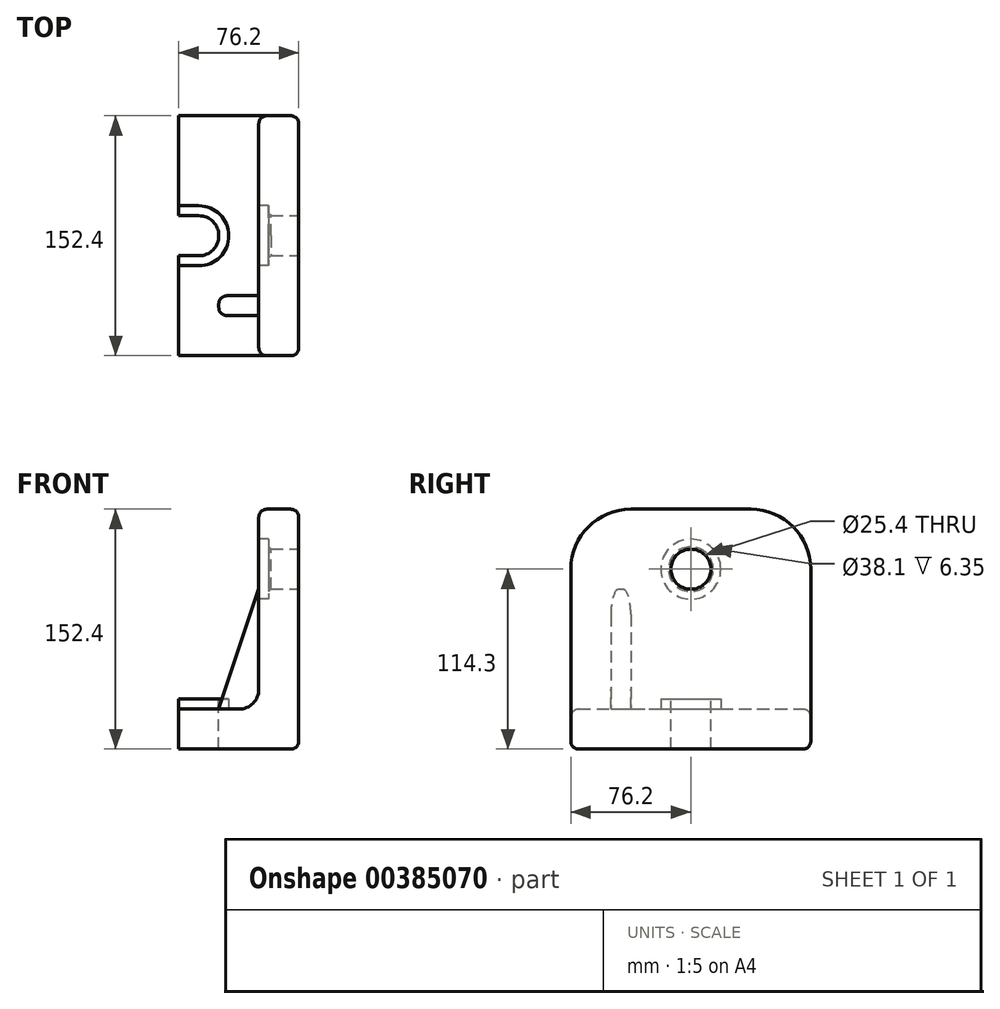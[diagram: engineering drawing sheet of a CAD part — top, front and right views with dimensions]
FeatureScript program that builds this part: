
annotation { "Feature Type Name" : "Feature", "Feature Type Description" : "" }
export const myFeature = defineFeature(function(context is Context, id is Id, definition is map)
    precondition{}
    {
        {
            var Q0;
            Q0=qCreatedBy(makeId("Front.planeOp"),FACE);
            var sketch = newSketch(context, id + "F0", { "sketchPlane" : qUnion([Q0])});
            skLineSegment(sketch, "E0", {"start": v(0, 0) * mm, "end": v(0, 152.4) * mm});
            skLineSegment(sketch, "E1", {"start": v(0, 152.4) * mm, "end": v(-25.4, 152.4) * mm});
            skLineSegment(sketch, "E2", {"start": v(-25.4, 152.4) * mm, "end": v(-25.4, 25.4) * mm});
            skLineSegment(sketch, "E3", {"start": v(-25.4, 25.4) * mm, "end": v(-76.2, 25.4) * mm});
            skLineSegment(sketch, "E4", {"start": v(-76.2, 25.4) * mm, "end": v(-76.2, 0) * mm});
            skLineSegment(sketch, "E5", {"start": v(-76.2, 0) * mm, "end": v(0, 0) * mm});
            skSolve(sketch);
        }
        {
            var Q0;
            Q0 = qSketchRegion(id + "F0", true);
            extrude(context, id + "F1", {"entities" : qUnion([Q0]), "endBound" : BoundingType.SYMMETRIC, "depth" : 152.4 * mm});
        }
        {
            var Q0;
            Q0=makeQuery(id+"F1.opExtrude","SWEPT_FACE",FACE,{"disambiguationData":[OSD([sQuery(id+"F0.wireOp",EDGE,"E0")])]});
            var sketch = newSketch(context, id + "F2", { "sketchPlane" : qUnion([Q0])});
            skCircle(sketch, "E6", {"center": v(0, 114.3) * mm, "radius": 12.7 * mm});
            skSolve(sketch);
        }
        {
            var Q0;
            Q0 = qSketchRegion(id + "F2", true);
            var Q1;
            Q1=makeQuery(id+"F1.opExtrude","SWEPT_FACE",FACE,{"disambiguationData":[OSD([sQuery(id+"F0.wireOp",EDGE,"E2")])]});
            extrude(context, id + "F3", {"entities" : qUnion([Q0]), "operationType" : NewBodyOperationType.REMOVE, "endBound" : BoundingType.UP_TO_SURFACE, "oppositeDirection" : true, "endBoundEntityFace" : qUnion([Q1]), "depth" : 25.4 * mm});
        }
        {
            var Q0;
            Q0=makeQuery(id+"F1.opExtrude","SWEPT_FACE",FACE,{"disambiguationData":[OSD([sQuery(id+"F0.wireOp",EDGE,"E3")])]});
            var sketch = newSketch(context, id + "F4", { "sketchPlane" : qUnion([Q0])});
            skLineSegment(sketch, "E7.bottom", {"start": v(-76.2, 12.7) * mm, "end": v(-63.5, 12.7) * mm});
            skLineSegment(sketch, "E7.top", {"start": v(-76.2, -12.7) * mm, "end": v(-63.5, -12.7) * mm});
            skLineSegment(sketch, "E7.left", {"start": v(-76.2, 12.7) * mm, "end": v(-76.2, -12.7) * mm});
            skArc(sketch, "E8", {"start": v(-63.5, -12.7) * mm, "mid": v(-50.8, 0) * mm, "end": v(-63.5, 12.7) * mm});
            skSolve(sketch);
        }
        {
            var Q0;
            Q0 = qSketchRegion(id + "F4", true);
            var Q1;
            Q1=makeQuery(id+"F1.opExtrude","SWEPT_FACE",FACE,{"disambiguationData":[OSD([sQuery(id+"F0.wireOp",EDGE,"E5")])]});
            extrude(context, id + "F5", {"entities" : qUnion([Q0]), "operationType" : NewBodyOperationType.REMOVE, "endBound" : BoundingType.UP_TO_SURFACE, "oppositeDirection" : true, "endBoundEntityFace" : qUnion([Q1]), "depth" : 25.4 * mm});
        }
        {
            var Q0;
            Q0=qCreatedBy(makeId("Front.planeOp"),FACE);
            cPlane(context, id + "F6", {"entities" : qUnion([Q0]), "cplaneType" : CPlaneType.OFFSET, "offset" : 44.45 * mm, "width" : 152.4 * mm, "height" : 152.4 * mm});
        }
        {
            var Q0;
            Q0=qCreatedBy(id+"F6.planeOp",FACE);
            var sketch = newSketch(context, id + "F7", { "sketchPlane" : qUnion([Q0])});
            skLineSegment(sketch, "E9.0.0", {"start": v(-25.4, 101.6) * mm, "end": v(-25.4, 25.4) * mm});
            skLineSegment(sketch, "E9.0.2", {"start": v(-25.4, 25.4) * mm, "end": v(-25.4, 101.6) * mm});
            skLineSegment(sketch, "E10.0.4", {"start": v(-25.4, 25.4) * mm, "end": v(-50.8, 25.4) * mm});
            skPoint(sketch, "E10.0.7.end.orphan", {"position": v(-50.8, 25.4) * mm});
            skLineSegment(sketch, "E11", {"start": v(-25.4, 101.6) * mm, "end": v(-50.8, 25.4) * mm});
            skSolve(sketch);
        }
        {
            var Q0;
            Q0 = qSketchRegion(id + "F7", true);
            extrude(context, id + "F8", {"entities" : qUnion([Q0]), "operationType" : NewBodyOperationType.ADD, "endBound" : BoundingType.SYMMETRIC, "depth" : 12.7 * mm});
        }
        {
            var Q0;
            Q0=makeQuery(id+"F1.opExtrude","CAP_EDGE",EDGE,{"disambiguationData":[OSD([sQuery(id+"F0.wireOp",EDGE,"E1")])],"isStart":false});
            var Q1;
            Q1=makeQuery(id+"F1.opExtrude","CAP_EDGE",EDGE,{"disambiguationData":[OSD([sQuery(id+"F0.wireOp",EDGE,"E1")])],"isStart":true});
            fillet(context, id + "F9", {"entities" : qUnion([Q0, Q1]), "radius" : 38.1 * mm, "tangentPropagation" : true, "allowEdgeOverflow" : false});
        }
        {
            var Q0;
            Q0=makeQuery(id+"F1.opExtrude","SWEPT_FACE",FACE,{"disambiguationData":[OSD([sQuery(id+"F0.wireOp",EDGE,"E2")])]});
            var sketch = newSketch(context, id + "F10", { "sketchPlane" : qUnion([Q0])});
            skCircle(sketch, "E12", {"center": v(0, 114.3) * mm, "radius": 19.05 * mm});
            skSolve(sketch);
        }
        {
            var Q0;
            Q0 = qSketchRegion(id + "F10", true);
            extrude(context, id + "F11", {"entities" : qUnion([Q0]), "operationType" : NewBodyOperationType.REMOVE, "oppositeDirection" : true, "depth" : 6.35 * mm});
        }
        {
            var Q0;
            Q0=makeQuery(id+"F11.boolean.opBoolean","INTERSECT",EDGE,{"derivedFrom":[makeQuery(id+"F3.boolean.opBoolean","COPY",FACE,{"derivedFrom":makeQuery(id+"F3.opExtrude","SWEPT_FACE",FACE,{"disambiguationData":[OSD([sQuery(id+"F2.wireOp",EDGE,"E6")])]})}),makeQuery(id+"F11.opExtrude","CAP_FACE",FACE,{"disambiguationData":[OSD([sQuery(id+"F10.wireOp",EDGE,"E12")])],"isStart":false})]});
            var Q1;
            Q1=makeQuery(id+"F11.boolean.opBoolean","COPY",EDGE,{"derivedFrom":makeQuery(id+"F11.opExtrude","CAP_EDGE",EDGE,{"disambiguationData":[OSD([sQuery(id+"F10.wireOp",EDGE,"E12")])],"isStart":true})});
            chamfer(context, id + "F12", {"entities" : qUnion([Q0, Q1]), "width" : 1.52 * mm, "tangentPropagation" : true});
        }
        {
            var Q0;
            Q0=makeQuery(id+"F9.opFillet","BLEND_EDGE",EDGE,{"blendedFrom":[makeQuery(id+"F1.opExtrude","CAP_EDGE",EDGE,{"disambiguationData":[OSD([sQuery(id+"F0.wireOp",EDGE,"E1")])],"isStart":false}),makeQuery(id+"F1.opExtrude","SWEPT_FACE",FACE,{"disambiguationData":[OSD([sQuery(id+"F0.wireOp",EDGE,"E2")])]})],"blendedInto":[makeQuery(id+"F1.opExtrude","SWEPT_FACE",FACE,{"disambiguationData":[OSD([sQuery(id+"F0.wireOp",EDGE,"E2")])]})]});
            fillet(context, id + "F13", {"entities" : qUnion([Q0]), "radius" : 5.08 * mm, "tangentPropagation" : true, "allowEdgeOverflow" : false});
        }
        {
            var Q0;
            Q0=makeQuery(id+"F1.opExtrude","SWEPT_FACE",FACE,{"disambiguationData":[OSD([sQuery(id+"F0.wireOp",EDGE,"E3")])]});
            var sketch = newSketch(context, id + "F14", { "sketchPlane" : qUnion([Q0])});
            skLineSegment(sketch, "E13.0", {"start": v(-76.2, -19.05) * mm, "end": v(-63.5, -19.05) * mm});
            skArc(sketch, "E13.1", {"start": v(-63.5, -19.05) * mm, "mid": v(-44.45, 0) * mm, "end": v(-63.5, 19.05) * mm});
            skLineSegment(sketch, "E13.2", {"start": v(-76.2, 19.05) * mm, "end": v(-63.5, 19.05) * mm});
            skLineSegment(sketch, "E14", {"start": v(-76.2, 19.05) * mm, "end": v(-76.2, 12.7) * mm});
            skLineSegment(sketch, "E15", {"start": v(-76.2, 12.7) * mm, "end": v(-63.5, 12.7) * mm});
            skLineSegment(sketch, "E16", {"start": v(-76.2, -19.05) * mm, "end": v(-76.2, -12.7) * mm});
            skLineSegment(sketch, "E17", {"start": v(-76.2, -12.7) * mm, "end": v(-63.5, -12.7) * mm});
            skArc(sketch, "E18", {"start": v(-63.5, -12.7) * mm, "mid": v(-50.8, 0) * mm, "end": v(-63.5, 12.7) * mm});
            skSolve(sketch);
        }
        {
            var Q0;
            Q0 = qSketchRegion(id + "F14", true);
            extrude(context, id + "F15", {"entities" : qUnion([Q0]), "operationType" : NewBodyOperationType.ADD, "depth" : 6.35 * mm});
        }
        {
            var Q0;
            Q0=makeQuery(id+"F9.opFillet","BLEND_EDGE",EDGE,{"blendedFrom":[makeQuery(id+"F1.opExtrude","CAP_EDGE",EDGE,{"disambiguationData":[OSD([sQuery(id+"F0.wireOp",EDGE,"E1")])],"isStart":false}),makeQuery(id+"F1.opExtrude","SWEPT_FACE",FACE,{"disambiguationData":[OSD([sQuery(id+"F0.wireOp",EDGE,"E0")])]})],"blendedInto":[makeQuery(id+"F1.opExtrude","SWEPT_FACE",FACE,{"disambiguationData":[OSD([sQuery(id+"F0.wireOp",EDGE,"E0")])]})]});
            var Q1;
            Q1=makeQuery(id+"F15.opExtrude","CAP_EDGE",EDGE,{"disambiguationData":[OSD([sQuery(id+"F14.wireOp",EDGE,"E13.0")])],"isStart":true});
            var Q2;
            Q2=makeQuery(id+"F8.opExtrude","CAP_EDGE",EDGE,{"disambiguationData":[OSD([sQuery(id+"F7.wireOp",EDGE,"E11")])],"isStart":false});
            var Q3;
            Q3=makeQuery(id+"F1nKhzs5GaQ9v0H_1.1.F8.opExtrude","CAP_EDGE",EDGE,{"disambiguationData":[OSD([sQuery(id+"F7.wireOp",EDGE,"E11")])],"isStart":false});
            var Q4;
            Q4=makeQuery(id+"F1nKhzs5GaQ9v0H_1.1.F8.opExtrude","CAP_EDGE",EDGE,{"disambiguationData":[OSD([sQuery(id+"F7.wireOp",EDGE,"E11")])],"isStart":true});
            var Q5;
            Q5=makeQuery(id+"F8.opExtrude","CAP_EDGE",EDGE,{"disambiguationData":[OSD([sQuery(id+"F7.wireOp",EDGE,"E11")])],"isStart":true});
            var Q6;
            Q6=makeQuery(id+"F1nKhzs5GaQ9v0H_1.1.F8.opExtrude","SWEPT_EDGE",EDGE,{"disambiguationData":[OSD([sQuery(id+"F7.wireOp",EDGE,"E10.0.4"),sQuery(id+"F7.wireOp",EDGE,"E11")])]});
            var Q7;
            Q7=makeQuery(id+"F8.opExtrude","SWEPT_EDGE",EDGE,{"disambiguationData":[OSD([sQuery(id+"F7.wireOp",EDGE,"E10.0.4"),sQuery(id+"F7.wireOp",EDGE,"E11")])]});
            var Q8;
            Q8=makeQuery(id+"F8.opExtrude","CAP_EDGE",EDGE,{"disambiguationData":[OSD([sQuery(id+"F7.wireOp",EDGE,"E9.0.2")])],"isStart":false});
            var Q9;
            Q9=makeQuery(id+"F1nKhzs5GaQ9v0H_1.1.F8.opExtrude","CAP_EDGE",EDGE,{"disambiguationData":[OSD([sQuery(id+"F7.wireOp",EDGE,"E9.0.2")])],"isStart":true});
            fillet(context, id + "F16", {"entities" : qUnion([Q0, Q1, Q2, Q3, Q4, Q5, Q6, Q7, Q8, Q9]), "radius" : 5.08 * mm, "tangentPropagation" : true, "allowEdgeOverflow" : false});
        }
        {
            var Q0;
            {var subQ0=sQuery(id+"F0.wireOp",EDGE,"E2");var subQ2=sQuery(id+"F7.wireOp",EDGE,"E11");var subQ3=sQuery(id+"F7.wireOp",EDGE,"E10.0.4");var subQ4=sQuery(id+"F7.wireOp",EDGE,"E9.0.2");var subQ5=makeQuery(id+"F8.opExtrude","CAP_FACE",FACE,{"disambiguationData":[OSD([subQ4,subQ3,subQ2])],"isStart":true});var subQ6=sQuery(id+"F0.wireOp",EDGE,"E3");Q0=makeQuery(id+"F1nKhzs5GaQ9v0H_1.1.F8.boolean.opBoolean","SPLIT",EDGE,{"disambiguationData":[TD([subQ5])],"derivedFrom":makeQuery(id+"F8.boolean.opBoolean","SPLIT",EDGE,{"disambiguationData":[TD([subQ5])],"derivedFrom":makeQuery(id+"F1.opExtrude","SWEPT_EDGE",EDGE,{"disambiguationData":[OSD([subQ0,subQ6])]})})});}
            var Q1;
            {var subQ0=sQuery(id+"F0.wireOp",EDGE,"E3");var subQ1=sQuery(id+"F0.wireOp",EDGE,"E2");Q1=makeQuery(id+"F8.boolean.opBoolean","SPLIT",EDGE,{"disambiguationData":[TD([makeQuery(id+"F8.opExtrude","CAP_FACE",FACE,{"disambiguationData":[OSD([sQuery(id+"F7.wireOp",EDGE,"E9.0.2"),sQuery(id+"F7.wireOp",EDGE,"E10.0.4"),sQuery(id+"F7.wireOp",EDGE,"E11")])],"isStart":false})])],"derivedFrom":makeQuery(id+"F1.opExtrude","SWEPT_EDGE",EDGE,{"disambiguationData":[OSD([subQ1,subQ0])]})});}
            var Q2;
            {var subQ0=sQuery(id+"F0.wireOp",EDGE,"E3");var subQ1=sQuery(id+"F0.wireOp",EDGE,"E2");var subQ5=sQuery(id+"F7.wireOp",EDGE,"E11");var subQ6=sQuery(id+"F7.wireOp",EDGE,"E10.0.4");var subQ7=sQuery(id+"F7.wireOp",EDGE,"E9.0.2");Q2=makeQuery(id+"F1nKhzs5GaQ9v0H_1.1.F8.boolean.opBoolean","SPLIT",EDGE,{"disambiguationData":[TD([makeQuery(id+"F1nKhzs5GaQ9v0H_1.1.F8.opExtrude","CAP_FACE",FACE,{"disambiguationData":[OSD([subQ7,subQ6,subQ5])],"isStart":false})])],"derivedFrom":makeQuery(id+"F8.boolean.opBoolean","SPLIT",EDGE,{"disambiguationData":[TD([makeQuery(id+"F8.opExtrude","CAP_FACE",FACE,{"disambiguationData":[OSD([subQ7,subQ6,subQ5])],"isStart":true})])],"derivedFrom":makeQuery(id+"F1.opExtrude","SWEPT_EDGE",EDGE,{"disambiguationData":[OSD([subQ1,subQ0])]})})});}
            fillet(context, id + "F17", {"entities" : qUnion([Q0, Q1, Q2]), "radius" : 12.7 * mm, "tangentPropagation" : true, "allowEdgeOverflow" : false});
        }
        {
            var Q0;
            Q0=makeQuery(id+"F1.opExtrude","CAP_EDGE",EDGE,{"disambiguationData":[OSD([sQuery(id+"F0.wireOp",EDGE,"E3")])],"isStart":true});
            var Q1;
            Q1=makeQuery(id+"F1.opExtrude","CAP_EDGE",EDGE,{"disambiguationData":[OSD([sQuery(id+"F0.wireOp",EDGE,"E3")])],"isStart":false});
            var Q2;
            Q2=makeQuery(id+"F1.opExtrude","CAP_EDGE",EDGE,{"disambiguationData":[OSD([sQuery(id+"F0.wireOp",EDGE,"E5")])],"isStart":false});
            fillet(context, id + "F18", {"entities" : qUnion([Q0, Q1, Q2]), "radius" : 5.08 * mm, "tangentPropagation" : true, "allowEdgeOverflow" : false});
        }
    });
